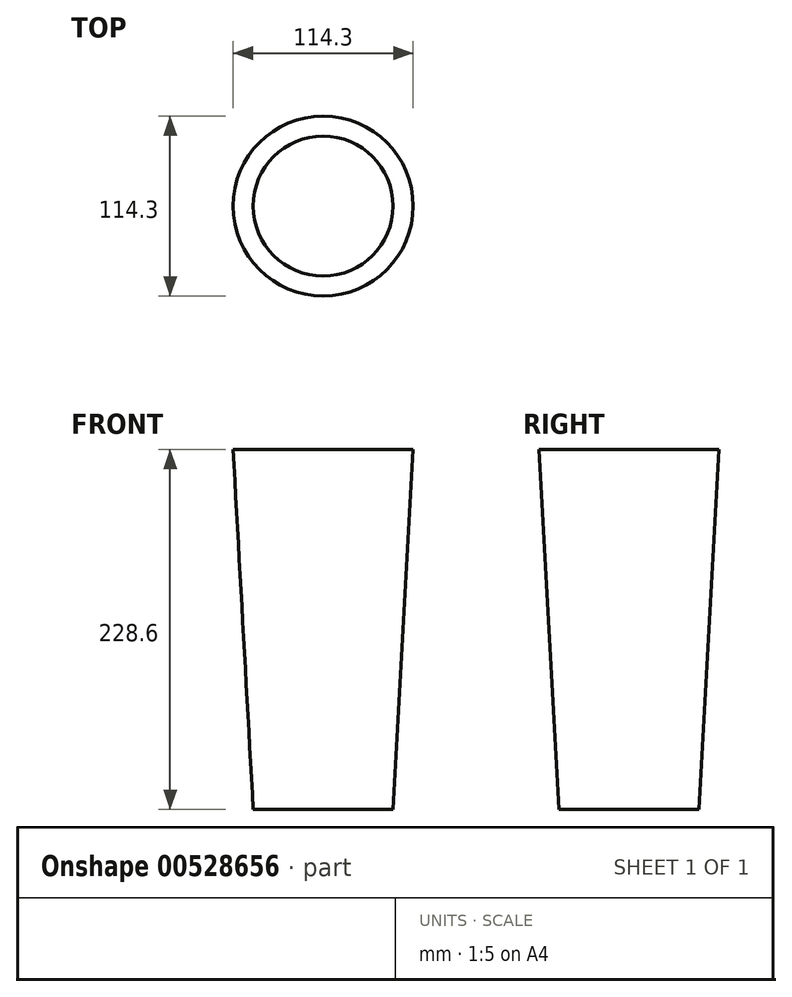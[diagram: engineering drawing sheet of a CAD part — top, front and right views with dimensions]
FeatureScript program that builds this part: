
annotation { "Feature Type Name" : "Feature", "Feature Type Description" : "" }
export const myFeature = defineFeature(function(context is Context, id is Id, definition is map)
    precondition{}
    {
        {
            var Q0;
            Q0=qCreatedBy(makeId("Front.planeOp"),FACE);
            var sketch = newSketch(context, id + "F0", { "sketchPlane" : qUnion([Q0])});
            skLineSegment(sketch, "E0", {"start": v(0, 114.3) * mm, "end": v(0, -114.3) * mm});
            skLineSegment(sketch, "E1", {"start": v(0, -114.3) * mm, "end": v(44.45, -114.3) * mm});
            skLineSegment(sketch, "E2", {"start": v(44.45, -114.3) * mm, "end": v(57.15, 114.3) * mm});
            skLineSegment(sketch, "E3", {"start": v(57.15, 114.3) * mm, "end": v(0, 114.3) * mm});
            skSolve(sketch);
        }
        {
            var Q0;
            Q0 = qSketchRegion(id + "F0", true);
            var Q1;
            Q1=sQuery(id+"F0.wireOp",EDGE,"E2");
            var Q2;
            Q2=sQuery(id+"F0.wireOp",EDGE,"E1");
            var Q3;
            Q3=sQuery(id+"F0.wireOp",EDGE,"E0");
            revolve(context, id + "F1", {"bodyType" : ToolBodyType.SURFACE, "entities" : qUnion([Q0]), "surfaceEntities" : qUnion([Q1, Q2]), "axis" : qUnion([Q3]), "revolveType" : RevolveType.FULL});
        }
    });
